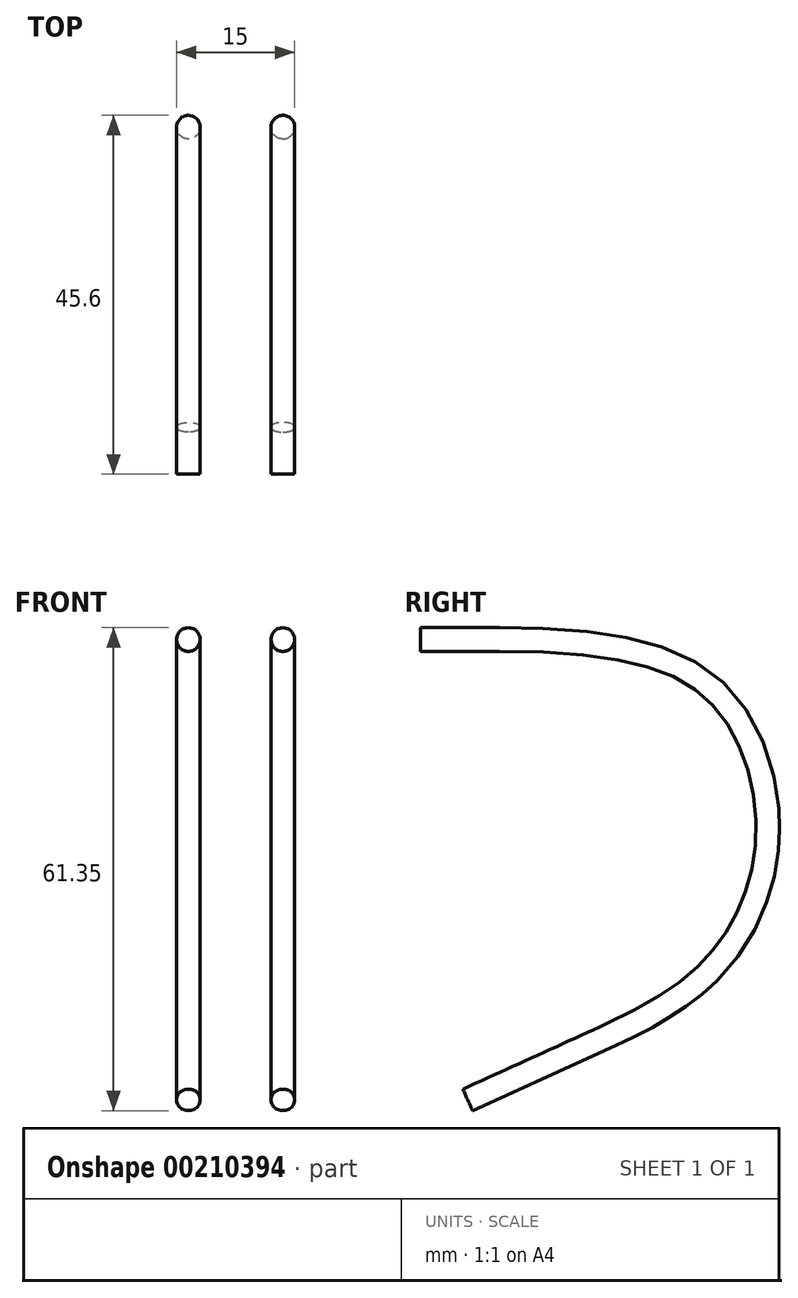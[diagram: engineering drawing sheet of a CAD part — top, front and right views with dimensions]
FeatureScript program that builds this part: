
annotation { "Feature Type Name" : "Feature", "Feature Type Description" : "" }
export const myFeature = defineFeature(function(context is Context, id is Id, definition is map)
    precondition{}
    {
        {
            var Q0;
            Q0=qCreatedBy(makeId("Right.planeOp"),FACE);
            cPlane(context, id + "F0", {"entities" : qUnion([Q0]), "cplaneType" : CPlaneType.OFFSET, "offset" : 6 * mm, "width" : 150 * mm, "height" : 150 * mm});
        }
        {
            var Q0;
            Q0=qCreatedBy(id+"F0.planeOp",FACE);
            var sketch = newSketch(context, id + "F1", { "sketchPlane" : qUnion([Q0])});
            skLineSegment(sketch, "E0", {"start": v(0, 0) * mm, "end": v(18.2, 8.27) * mm});
            skLineSegment(sketch, "E1", {"start": v(-5.97, 58.48) * mm, "end": v(4.03, 58.48) * mm});
            skFitSpline(sketch, "E2", {"points": [v(4.03, 58.48) * mm, v(31.94, 51.48) * mm, v(38.13, 34.32) * mm, v(33.34, 19.41) * mm, v(18.2, 8.27) * mm], "startDerivative": vector(138.06, 0) * mm, "endDerivative": vector(-90.84, -41.28) * mm});
            skSolve(sketch);
        }
        {
            var Q0;
            Q0=sQuery(id+"F1.wireOp",VERTEX,"E0.start");
            var Q1;
            Q1=sQuery(id+"F1.wireOp",EDGE,"E0");
            cPlane(context, id + "F2", {"entities" : qUnion([Q0, Q1]), "cplaneType" : CPlaneType.LINE_POINT, "offset" : 25 * mm, "width" : 150 * mm, "height" : 150 * mm});
        }
        {
            var Q0;
            Q0=qCreatedBy(id+"F2.planeOp",FACE);
            var sketch = newSketch(context, id + "F3", { "sketchPlane" : qUnion([Q0])});
            skCircle(sketch, "E3", {"center": v(-6, 0) * mm, "radius": 1.5 * mm});
            skSolve(sketch);
        }
        {
            var Q0;
            Q0=qSketchRegion(id+"F3",true);
            var Q1;
            Q1=qConstructionFilter(qBodyType(qCreatedBy(id+"F1",EDGE),BodyType.WIRE),ConstructionObject.NO);
            sweep(context, id + "F4", {"profiles" : qUnion([Q0]), "path" : qUnion([Q1])});
        }
        {
            var Q0;
            Q0=makeQuery(id+"F4.opSweep","SWEPT_BODY",BODY,{"disambiguationData":[OSD([sQuery(id+"F1.wireOp",EDGE,"E0"),sQuery(id+"F3.wireOp",EDGE,"E3")])]});
            var Q1;
            Q1=qCreatedBy(makeId("Right.planeOp"),FACE);
            mirror(context, id + "F5", {"entities" : qUnion([Q0]), "mirrorPlane" : qUnion([Q1])});
        }
    });
